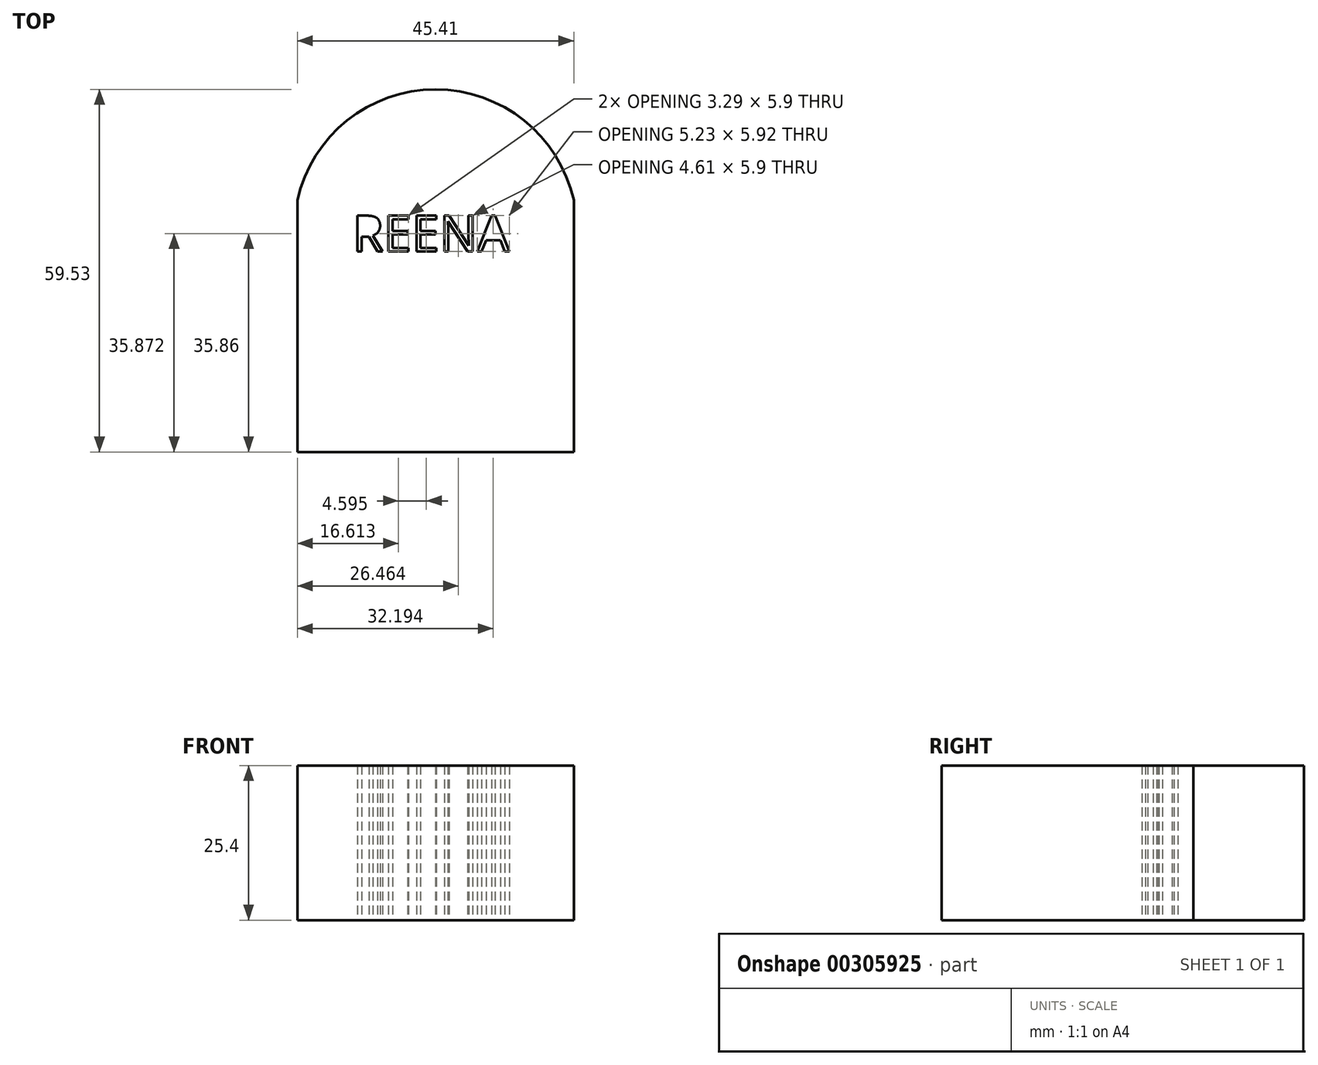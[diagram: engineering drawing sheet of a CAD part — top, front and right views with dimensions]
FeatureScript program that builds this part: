
annotation { "Feature Type Name" : "Feature", "Feature Type Description" : "" }
export const myFeature = defineFeature(function(context is Context, id is Id, definition is map)
    precondition{}
    {
        {
            var Q0;
            Q0=qCreatedBy(makeId("Top.planeOp"),FACE);
            var sketch = newSketch(context, id + "F0", { "sketchPlane" : qUnion([Q0])});
            skLineSegment(sketch, "E0", {"start": v(-35.37, -30.23) * mm, "end": v(-35.37, 11.14) * mm});
            skLineSegment(sketch, "E1", {"start": v(10.04, 11.14) * mm, "end": v(10.04, -30.23) * mm});
            skLineSegment(sketch, "E2", {"start": v(10.04, -30.23) * mm, "end": v(-35.37, -30.23) * mm});
            skArc(sketch, "E3", {"start": v(10.04, 11.14) * mm, "mid": v(-12.66, 29.3) * mm, "end": v(-35.37, 11.14) * mm});
            skLineSegment(sketch, "E4", {"start": v(-31.01, 11.14) * mm, "end": v(-31.01, -26.96) * mm});
            skLineSegment(sketch, "E5", {"start": v(-31.01, -26.96) * mm, "end": v(5.38, -26.96) * mm});
            skLineSegment(sketch, "E6", {"start": v(5.38, -26.96) * mm, "end": v(5.38, 11.14) * mm});
            skArc(sketch, "E7", {"start": v(5.38, 11.14) * mm, "mid": v(-12.82, 23.7) * mm, "end": v(-31.01, 11.14) * mm});
            skText(sketch, "E8", { "text": "REENA", "fontName": "OpenSans-Regular.ttf"});
            const initialGuessF0  = {"E8": [-0.02632, 0.00268, 1, 0, 0.00595]};
            skSetInitialGuess(sketch, initialGuessF0);
            skSolve(sketch);
        }
        {
            var Q0;
            Q0 = qSketchRegion(id + "F0", true);
            var Q1;
            Q1=makeQuery(id+"F0.imprint","IMPRINT",FACE,{"disambiguationData":[TD([[makeQuery(id+"F0.imprint","IMPRINT",EDGE,{"derivedFrom":sQuery(id+"F0.wireOp",EDGE,"E4")}),1.0]])]});
            extrude(context, id + "F1", {"entities" : qUnion([Q0, Q1]), "depth" : 25.4 * mm});
        }
        {
            var Q0;
            Q0 = qSketchRegion(id + "F0", true);
            extrude(context, id + "F2", {"entities" : qUnion([Q0]), "operationType" : NewBodyOperationType.ADD, "depth" : 25.4 * mm});
        }
    });
